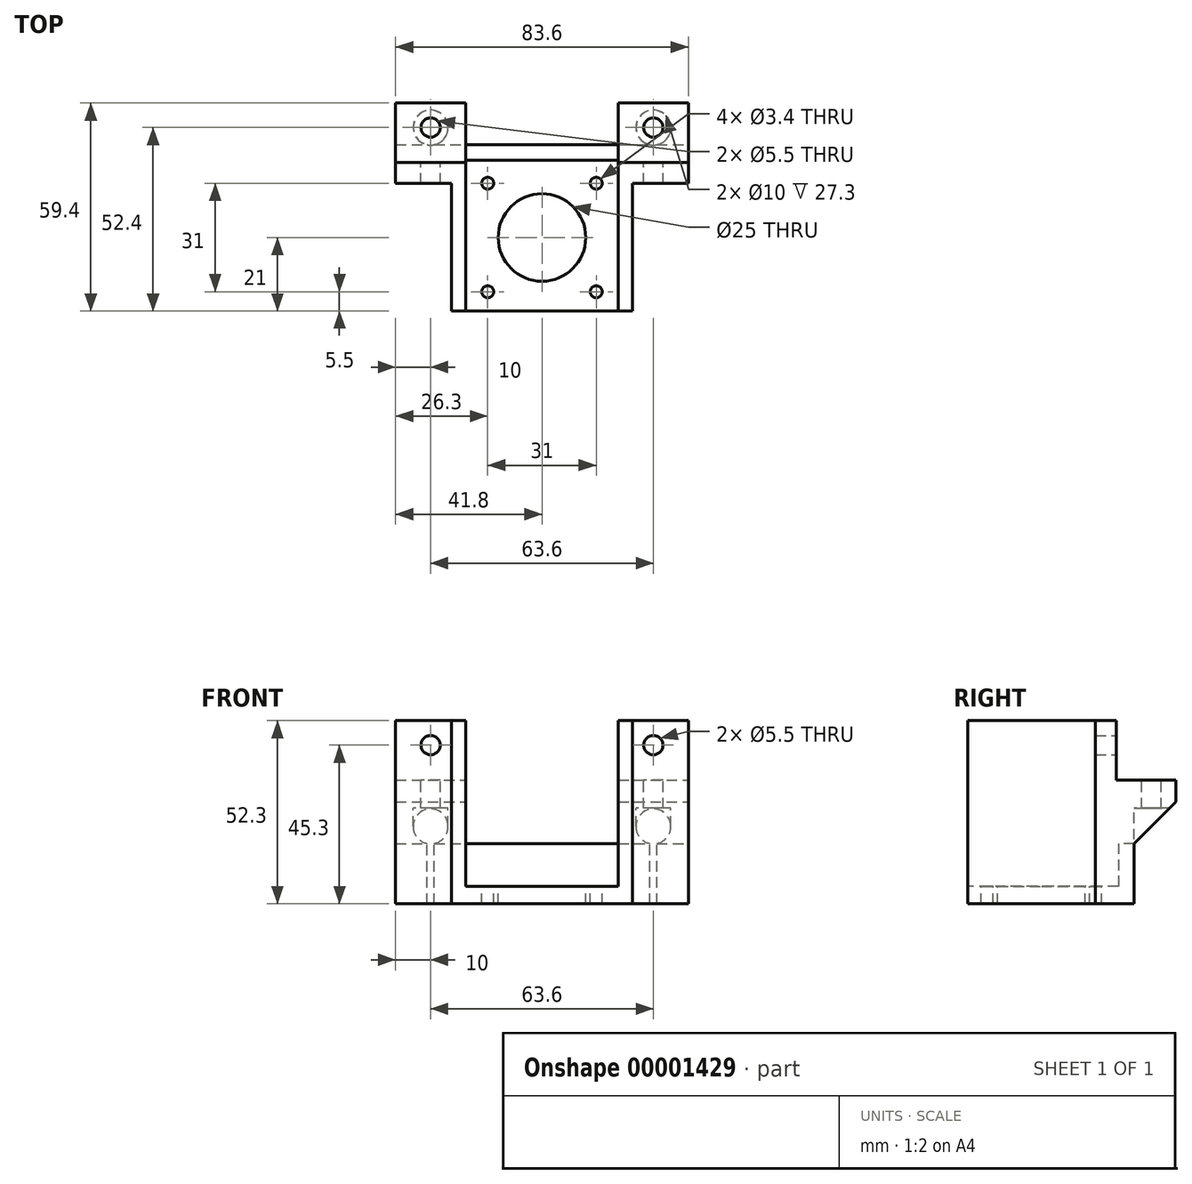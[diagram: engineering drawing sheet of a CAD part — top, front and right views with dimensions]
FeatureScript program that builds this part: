
annotation { "Feature Type Name" : "Feature", "Feature Type Description" : "" }
export const myFeature = defineFeature(function(context is Context, id is Id, definition is map)
    precondition{}
    {
        {
            var Q0;
            Q0=qCreatedBy(makeId("Top.planeOp"),FACE);
            var sketch = newSketch(context, id + "F0", { "sketchPlane" : qUnion([Q0])});
            skLineSegment(sketch, "E0", {"start": v(0, 0) * mm, "end": v(25.8, 0) * mm});
            skLineSegment(sketch, "E1", {"start": v(25.8, 0) * mm, "end": v(25.8, 36.4) * mm});
            skLineSegment(sketch, "E2", {"start": v(25.8, 36.4) * mm, "end": v(41.8, 36.4) * mm});
            skLineSegment(sketch, "E3", {"start": v(41.8, 36.4) * mm, "end": v(41.8, 42.4) * mm});
            skLineSegment(sketch, "E4", {"start": v(41.8, 42.4) * mm, "end": v(-41.8, 42.4) * mm});
            skLineSegment(sketch, "E5", {"start": v(-41.8, 42.4) * mm, "end": v(-41.8, 36.4) * mm});
            skLineSegment(sketch, "E6", {"start": v(-41.8, 36.4) * mm, "end": v(-25.8, 36.4) * mm});
            skLineSegment(sketch, "E7", {"start": v(-25.8, 36.4) * mm, "end": v(-25.8, 0) * mm});
            skLineSegment(sketch, "E8", {"start": v(-25.8, 0) * mm, "end": v(0, 0) * mm});
            skSolve(sketch);
        }
        {
            var Q0;
            Q0 = qSketchRegion(id + "F0", true);
            extrude(context, id + "F1", {"entities" : qUnion([Q0]), "depth" : 52.3 * mm});
        }
        {
            var Q0;
            Q0=makeQuery(id+"F1.opExtrude","SWEPT_FACE",FACE,{"disambiguationData":[OSD([sQuery(id+"F0.wireOp",EDGE,"E3")])]});
            var sketch = newSketch(context, id + "F2", { "sketchPlane" : qUnion([Q0])});
            skLineSegment(sketch, "E9", {"start": v(42.4, 35.3) * mm, "end": v(59.4, 35.3) * mm});
            skLineSegment(sketch, "E10", {"start": v(59.4, 35.3) * mm, "end": v(59.4, 29.1) * mm});
            skLineSegment(sketch, "E11", {"start": v(59.4, 29.1) * mm, "end": v(47.5, 17.2) * mm});
            skLineSegment(sketch, "E12", {"start": v(47.5, 17.2) * mm, "end": v(47.5, 0) * mm});
            skLineSegment(sketch, "E13", {"start": v(47.5, 0) * mm, "end": v(42.4, 0) * mm});
            skLineSegment(sketch, "E14", {"start": v(42.4, 0) * mm, "end": v(42.4, 35.3) * mm});
            skLineSegment(sketch, "E15.0", {"start": v(0, 52.3) * mm, "end": v(0, 0) * mm, "construction": true});
            skSolve(sketch);
        }
        {
            var Q0;
            Q0=makeQuery(id+"F2.imprint","IMPRINT",FACE,{"disambiguationData":[TD([[makeQuery(id+"F2.imprint","IMPRINT",EDGE,{"derivedFrom":sQuery(id+"F2.wireOp",EDGE,"E9")}),-1.0]])]});
            var Q1;
            Q1=makeQuery(id+"F1.opExtrude","SWEPT_FACE",FACE,{"disambiguationData":[OSD([sQuery(id+"F0.wireOp",EDGE,"E5")])]});
            extrude(context, id + "F3", {"entities" : qUnion([Q0]), "operationType" : NewBodyOperationType.ADD, "endBound" : BoundingType.UP_TO_SURFACE, "oppositeDirection" : true, "endBoundEntityFace" : qUnion([Q1]), "depth" : 25 * mm});
        }
        {
            var Q0;
            Q0=makeQuery(id+"F1.opExtrude","SWEPT_FACE",FACE,{"disambiguationData":[OSD([sQuery(id+"F0.wireOp",EDGE,"E8")])]});
            var sketch = newSketch(context, id + "F4", { "sketchPlane" : qUnion([Q0])});
            skLineSegment(sketch, "E16", {"start": v(-21.8, 52.3) * mm, "end": v(-21.8, 5) * mm});
            skLineSegment(sketch, "E17", {"start": v(-21.8, 5) * mm, "end": v(21.8, 5) * mm});
            skLineSegment(sketch, "E18", {"start": v(21.8, 5) * mm, "end": v(21.8, 52.3) * mm});
            skLineSegment(sketch, "E19", {"start": v(21.8, 52.3) * mm, "end": v(-21.8, 52.3) * mm});
            skLineSegment(sketch, "E20", {"start": v(0, 5) * mm, "end": v(0, 0) * mm, "construction": true});
            skSolve(sketch);
        }
        {
            var Q0;
            Q0=makeQuery(id+"F4.imprint","IMPRINT",FACE,{"disambiguationData":[TD([[makeQuery(id+"F4.imprint","IMPRINT",EDGE,{"derivedFrom":sQuery(id+"F4.wireOp",EDGE,"E16")}),1.0]])]});
            extrude(context, id + "F5", {"entities" : qUnion([Q0]), "operationType" : NewBodyOperationType.REMOVE, "endBound" : BoundingType.THROUGH_ALL, "oppositeDirection" : true, "depth" : 25 * mm});
        }
        {
            var Q0;
            Q0=makeQuery(id+"F5.boolean.opBoolean","COPY",FACE,{"derivedFrom":makeQuery(id+"F5.opExtrude","SWEPT_FACE",FACE,{"disambiguationData":[OSD([sQuery(id+"F4.wireOp",EDGE,"E16")])]})});
            var sketch = newSketch(context, id + "F6", { "sketchPlane" : qUnion([Q0])});
            skLineSegment(sketch, "E21", {"start": v(47.5, 17.2) * mm, "end": v(43, 17.2) * mm});
            skLineSegment(sketch, "E22", {"start": v(43, 17.2) * mm, "end": v(43, 5) * mm});
            skLineSegment(sketch, "E23", {"start": v(43, 5) * mm, "end": v(47.5, 5) * mm});
            skLineSegment(sketch, "E24", {"start": v(47.5, 5) * mm, "end": v(47.5, 17.2) * mm});
            skSolve(sketch);
        }
        {
            var Q0;
            Q0=makeQuery(id+"F6.imprint","IMPRINT",FACE,{"disambiguationData":[TD([[makeQuery(id+"F6.imprint","IMPRINT",EDGE,{"derivedFrom":sQuery(id+"F6.wireOp",EDGE,"E21")}),1.0]])]});
            var Q1;
            Q1=makeQuery(id+"F5.boolean.opBoolean","COPY",FACE,{"derivedFrom":makeQuery(id+"F5.opExtrude","SWEPT_FACE",FACE,{"disambiguationData":[OSD([sQuery(id+"F4.wireOp",EDGE,"E18")])]})});
            extrude(context, id + "F7", {"entities" : qUnion([Q0]), "operationType" : NewBodyOperationType.ADD, "endBound" : BoundingType.UP_TO_SURFACE, "endBoundEntityFace" : qUnion([Q1]), "depth" : 25 * mm});
        }
        {
            var Q0;
            {var subQ0=sQuery(id+"F0.wireOp",EDGE,"E4");var subQ2=sQuery(id+"F0.wireOp",EDGE,"E3");Q0=makeQuery(id+"F5.boolean.opBoolean","SPLIT",FACE,{"disambiguationData":[TD([makeQuery(id+"F1.opExtrude","SWEPT_FACE",FACE,{"disambiguationData":[OSD([subQ2])]})])],"derivedFrom":makeQuery(id+"F1.opExtrude","SWEPT_FACE",FACE,{"disambiguationData":[OSD([subQ0])]})});}
            var sketch = newSketch(context, id + "F8", { "sketchPlane" : qUnion([Q0])});
            skLineSegment(sketch, "E25", {"start": v(-31.8, 35.3) * mm, "end": v(-31.8, 45.3) * mm, "construction": true});
            skLineSegment(sketch, "E26.0", {"start": v(41.8, 35.3) * mm, "end": v(21.8, 35.3) * mm, "construction": true});
            skLineSegment(sketch, "E27", {"start": v(31.8, 35.3) * mm, "end": v(31.8, 45.3) * mm, "construction": true});
            skLineSegment(sketch, "E28", {"start": v(31.8, 45.3) * mm, "end": v(-31.8, 45.3) * mm, "construction": true});
            skCircle(sketch, "E29", {"center": v(-31.8, 45.3) * mm, "radius": 2.75 * mm});
            skCircle(sketch, "E30", {"center": v(31.8, 45.3) * mm, "radius": 2.75 * mm});
            skSolve(sketch);
        }
        {
            var Q0;
            {Q0=qUnion([makeQuery(id+"F8.imprint","IMPRINT",FACE,{"disambiguationData":[TD([[makeQuery(id+"F8.imprint","IMPRINT",EDGE,{"derivedFrom":sQuery(id+"F8.wireOp",EDGE,"E30")}),1.0]])]}),makeQuery(id+"F8.imprint","IMPRINT",FACE,{"disambiguationData":[TD([[makeQuery(id+"F8.imprint","IMPRINT",EDGE,{"derivedFrom":sQuery(id+"F8.wireOp",EDGE,"E29")}),1.0]])]})]);}
            extrude(context, id + "F9", {"entities" : qUnion([Q0]), "operationType" : NewBodyOperationType.REMOVE, "endBound" : BoundingType.THROUGH_ALL, "oppositeDirection" : true, "depth" : 25 * mm});
        }
        {
            var Q0;
            {var subQ0=sQuery(id+"F2.wireOp",EDGE,"E9");Q0=makeQuery(id+"F5.boolean.opBoolean","SPLIT",FACE,{"disambiguationData":[TD([makeQuery(id+"F1.opExtrude","SWEPT_FACE",FACE,{"disambiguationData":[OSD([sQuery(id+"F0.wireOp",EDGE,"E3")])]})])],"derivedFrom":makeQuery(id+"F3.opExtrude","SWEPT_FACE",FACE,{"disambiguationData":[OSD([subQ0])]})});}
            var sketch = newSketch(context, id + "F10", { "sketchPlane" : qUnion([Q0])});
            skLineSegment(sketch, "E31", {"start": v(31.8, 42.4) * mm, "end": v(31.8, 52.4) * mm, "construction": true});
            skLineSegment(sketch, "E32.0", {"start": v(-21.8, 42.4) * mm, "end": v(-41.8, 42.4) * mm, "construction": true});
            skLineSegment(sketch, "E33", {"start": v(-31.8, 42.4) * mm, "end": v(-31.8, 52.4) * mm, "construction": true});
            skLineSegment(sketch, "E34", {"start": v(-31.8, 52.4) * mm, "end": v(31.8, 52.4) * mm, "construction": true});
            skCircle(sketch, "E35", {"center": v(31.8, 52.4) * mm, "radius": 2.75 * mm});
            skCircle(sketch, "E36", {"center": v(-31.8, 52.4) * mm, "radius": 2.75 * mm});
            skSolve(sketch);
        }
        {
            var Q0;
            {Q0=qUnion([makeQuery(id+"F10.imprint","IMPRINT",FACE,{"disambiguationData":[TD([[makeQuery(id+"F10.imprint","IMPRINT",EDGE,{"derivedFrom":sQuery(id+"F10.wireOp",EDGE,"E36")}),1.0]])]}),makeQuery(id+"F10.imprint","IMPRINT",FACE,{"disambiguationData":[TD([[makeQuery(id+"F10.imprint","IMPRINT",EDGE,{"derivedFrom":sQuery(id+"F10.wireOp",EDGE,"E35")}),1.0]])]})]);}
            extrude(context, id + "F11", {"entities" : qUnion([Q0]), "operationType" : NewBodyOperationType.REMOVE, "endBound" : BoundingType.THROUGH_ALL, "oppositeDirection" : true, "depth" : 25 * mm});
        }
        {
            var Q0;
            {var subQ0=sQuery(id+"F2.wireOp",EDGE,"E9");Q0=makeQuery(id+"F5.boolean.opBoolean","SPLIT",FACE,{"disambiguationData":[TD([makeQuery(id+"F1.opExtrude","SWEPT_FACE",FACE,{"disambiguationData":[OSD([sQuery(id+"F0.wireOp",EDGE,"E3")])]})])],"derivedFrom":makeQuery(id+"F3.opExtrude","SWEPT_FACE",FACE,{"disambiguationData":[OSD([subQ0])]})});}
            cPlane(context, id + "F12", {"entities" : qUnion([Q0]), "cplaneType" : CPlaneType.OFFSET, "offset" : 8 * mm, "oppositeDirection" : true, "width" : 150 * mm, "height" : 150 * mm});
        }
        {
            var Q0;
            Q0=qCreatedBy(id+"F12.planeOp",FACE);
            var sketch = newSketch(context, id + "F13", { "sketchPlane" : qUnion([Q0])});
            skCircle(sketch, "E37.0", {"center": v(31.8, 52.4) * mm, "radius": 2.75 * mm, "construction": true});
            skCircle(sketch, "E38.0", {"center": v(-31.8, 52.4) * mm, "radius": 2.75 * mm, "construction": true});
            skCircle(sketch, "E39", {"center": v(31.8, 52.4) * mm, "radius": 5 * mm});
            skCircle(sketch, "E40", {"center": v(-31.8, 52.4) * mm, "radius": 5 * mm});
            skSolve(sketch);
        }
        {
            var Q0;
            {Q0=qUnion([makeQuery(id+"F13.imprint","IMPRINT",FACE,{"disambiguationData":[TD([[makeQuery(id+"F13.imprint","IMPRINT",EDGE,{"derivedFrom":sQuery(id+"F13.wireOp",EDGE,"E39")}),1.0]])]}),makeQuery(id+"F13.imprint","IMPRINT",FACE,{"disambiguationData":[TD([[makeQuery(id+"F13.imprint","IMPRINT",EDGE,{"derivedFrom":sQuery(id+"F13.wireOp",EDGE,"E40")}),1.0]])]})]);}
            extrude(context, id + "F14", {"entities" : qUnion([Q0]), "operationType" : NewBodyOperationType.REMOVE, "endBound" : BoundingType.THROUGH_ALL, "oppositeDirection" : true, "depth" : 25 * mm});
        }
        {
            var Q0;
            Q0=makeQuery(id+"F5.boolean.opBoolean","COPY",FACE,{"derivedFrom":makeQuery(id+"F5.opExtrude","SWEPT_FACE",FACE,{"disambiguationData":[OSD([sQuery(id+"F4.wireOp",EDGE,"E17")])]})});
            var sketch = newSketch(context, id + "F15", { "sketchPlane" : qUnion([Q0])});
            skLineSegment(sketch, "E41", {"start": v(0, 0) * mm, "end": v(0, 21) * mm, "construction": true});
            skLineSegment(sketch, "E42", {"start": v(0, 21) * mm, "end": v(0, 43) * mm, "construction": true});
            skCircle(sketch, "E43", {"center": v(0, 21) * mm, "radius": 12.5 * mm});
            skLineSegment(sketch, "E44.rect.bottom", {"start": v(-15.5, 36.5) * mm, "end": v(15.5, 36.5) * mm, "construction": true});
            skLineSegment(sketch, "E44.rect.top", {"start": v(-15.5, 5.5) * mm, "end": v(15.5, 5.5) * mm, "construction": true});
            skLineSegment(sketch, "E44.rect.left", {"start": v(-15.5, 36.5) * mm, "end": v(-15.5, 5.5) * mm, "construction": true});
            skLineSegment(sketch, "E44.rect.right", {"start": v(15.5, 36.5) * mm, "end": v(15.5, 5.5) * mm, "construction": true});
            skCircle(sketch, "E45", {"center": v(-15.5, 36.5) * mm, "radius": 1.7 * mm});
            skCircle(sketch, "E46", {"center": v(15.5, 36.5) * mm, "radius": 1.7 * mm});
            skCircle(sketch, "E47", {"center": v(15.5, 5.5) * mm, "radius": 1.7 * mm});
            skCircle(sketch, "E48", {"center": v(-15.5, 5.5) * mm, "radius": 1.7 * mm});
            skSolve(sketch);
        }
        {
            var Q0;
            {Q0=qUnion([makeQuery(id+"F15.imprint","IMPRINT",FACE,{"disambiguationData":[TD([[makeQuery(id+"F15.imprint","IMPRINT",EDGE,{"derivedFrom":sQuery(id+"F15.wireOp",EDGE,"E43")}),1.0]])]}),makeQuery(id+"F15.imprint","IMPRINT",FACE,{"disambiguationData":[TD([[makeQuery(id+"F15.imprint","IMPRINT",EDGE,{"derivedFrom":sQuery(id+"F15.wireOp",EDGE,"E45")}),1.0]])]}),makeQuery(id+"F15.imprint","IMPRINT",FACE,{"disambiguationData":[TD([[makeQuery(id+"F15.imprint","IMPRINT",EDGE,{"derivedFrom":sQuery(id+"F15.wireOp",EDGE,"E46")}),1.0]])]}),makeQuery(id+"F15.imprint","IMPRINT",FACE,{"disambiguationData":[TD([[makeQuery(id+"F15.imprint","IMPRINT",EDGE,{"derivedFrom":sQuery(id+"F15.wireOp",EDGE,"E47")}),1.0]])]}),makeQuery(id+"F15.imprint","IMPRINT",FACE,{"disambiguationData":[TD([[makeQuery(id+"F15.imprint","IMPRINT",EDGE,{"derivedFrom":sQuery(id+"F15.wireOp",EDGE,"E48")}),1.0]])]})]);}
            extrude(context, id + "F16", {"entities" : qUnion([Q0]), "operationType" : NewBodyOperationType.REMOVE, "endBound" : BoundingType.THROUGH_ALL, "oppositeDirection" : true, "depth" : 25 * mm});
        }
    });
